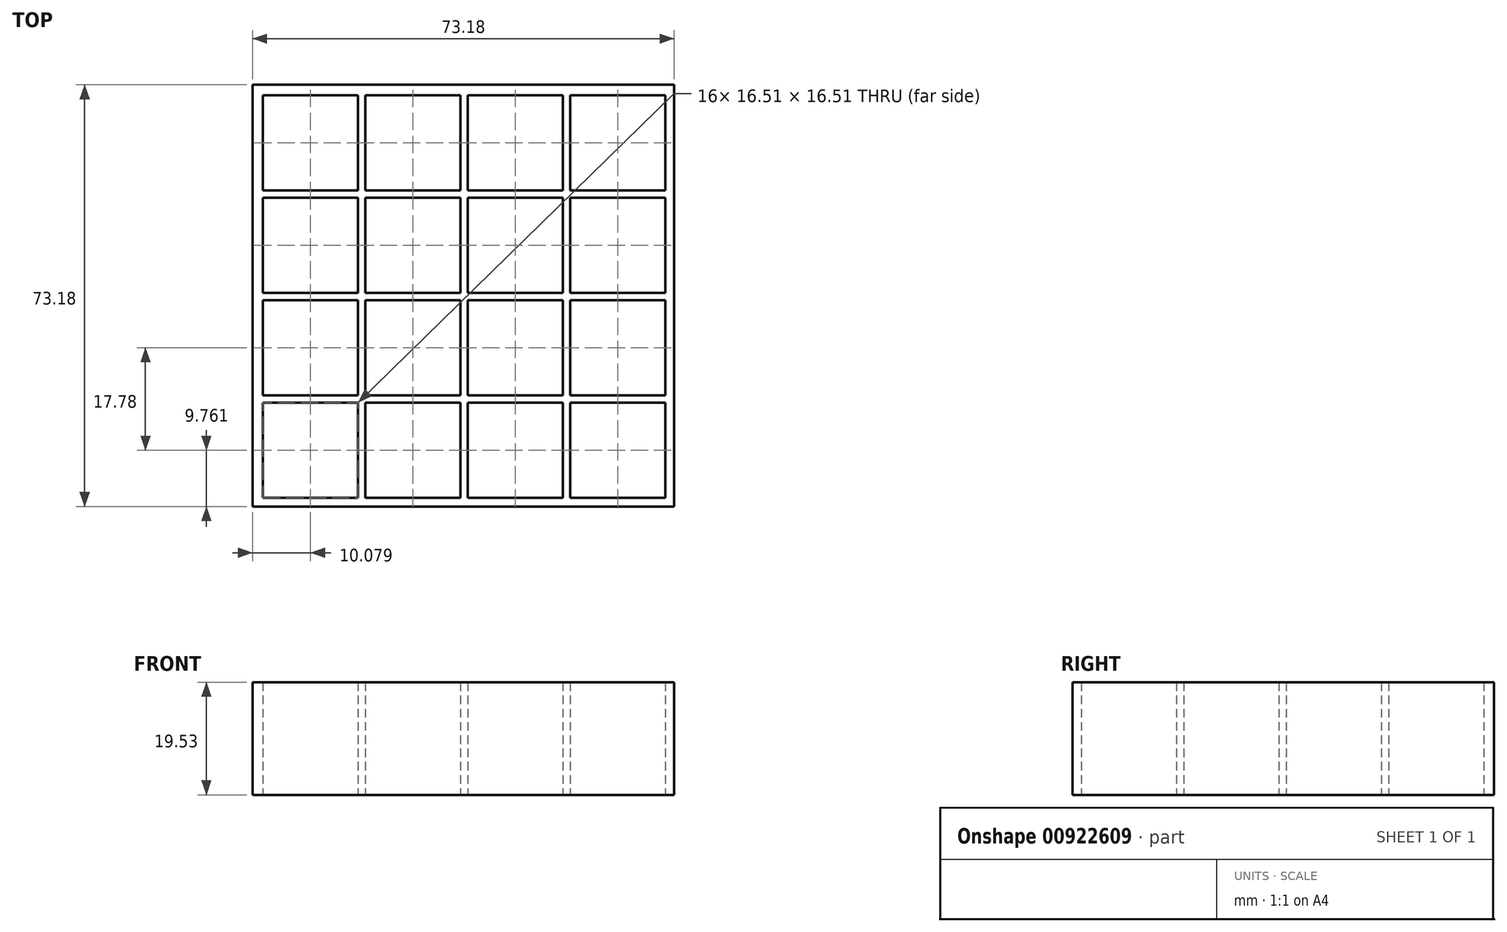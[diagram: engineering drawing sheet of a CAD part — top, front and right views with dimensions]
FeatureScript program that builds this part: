
annotation { "Feature Type Name" : "Feature", "Feature Type Description" : "" }
export const myFeature = defineFeature(function(context is Context, id is Id, definition is map)
    precondition{}
    {
        {
            var Q0;
            Q0=qCreatedBy(makeId("Top.planeOp"),FACE);
            var sketch = newSketch(context, id + "F0", { "sketchPlane" : qUnion([Q0])});
            skLineSegment(sketch, "E0.bottom", {"start": v(-731.84, 731.84) * mm, "end": v(731.84, 731.84) * mm});
            skLineSegment(sketch, "E0.top", {"start": v(-731.84, -731.84) * mm, "end": v(731.84, -731.84) * mm});
            skLineSegment(sketch, "E0.left", {"start": v(-731.84, 731.84) * mm, "end": v(-731.84, -731.84) * mm});
            skLineSegment(sketch, "E0.right", {"start": v(731.84, 731.84) * mm, "end": v(731.84, -731.84) * mm});
            skPoint(sketch, "E0.middle", {"position": v(0, 0) * mm});
            skLineSegment(sketch, "E1.bottom", {"start": v(-695.33, 695.33) * mm, "end": v(-365.13, 695.33) * mm});
            skLineSegment(sketch, "E1.top", {"start": v(-695.32, 365.13) * mm, "end": v(-365.12, 365.13) * mm});
            skLineSegment(sketch, "E1.left", {"start": v(-695.32, 695.33) * mm, "end": v(-695.32, 365.13) * mm});
            skLineSegment(sketch, "E1.right", {"start": v(-365.12, 695.33) * mm, "end": v(-365.12, 365.13) * mm});
            skLineSegment(sketch, "E2.0.1.0", {"start": v(-695.32, 339.73) * mm, "end": v(-695.32, 9.53) * mm});
            skLineSegment(sketch, "E2.0.1.1", {"start": v(-695.33, 339.73) * mm, "end": v(-365.13, 339.73) * mm});
            skLineSegment(sketch, "E2.0.1.2", {"start": v(-365.12, 339.73) * mm, "end": v(-365.12, 9.53) * mm});
            skLineSegment(sketch, "E2.0.1.3", {"start": v(-695.32, 9.53) * mm, "end": v(-365.12, 9.53) * mm});
            skLineSegment(sketch, "E2.0.2.0", {"start": v(-695.32, -15.87) * mm, "end": v(-695.32, -346.07) * mm});
            skLineSegment(sketch, "E2.0.2.1", {"start": v(-695.33, -15.87) * mm, "end": v(-365.13, -15.87) * mm});
            skLineSegment(sketch, "E2.0.2.2", {"start": v(-365.12, -15.87) * mm, "end": v(-365.12, -346.07) * mm});
            skLineSegment(sketch, "E2.0.2.3", {"start": v(-695.32, -346.07) * mm, "end": v(-365.12, -346.07) * mm});
            skLineSegment(sketch, "E2.0.3.0", {"start": v(-695.32, -371.48) * mm, "end": v(-695.32, -701.68) * mm});
            skLineSegment(sketch, "E2.0.3.1", {"start": v(-695.33, -371.48) * mm, "end": v(-365.13, -371.48) * mm});
            skLineSegment(sketch, "E2.0.3.2", {"start": v(-365.12, -371.48) * mm, "end": v(-365.12, -701.68) * mm});
            skLineSegment(sketch, "E2.0.3.3", {"start": v(-695.32, -701.68) * mm, "end": v(-365.12, -701.68) * mm});
            skLineSegment(sketch, "E2.1.0.0", {"start": v(-339.72, 695.33) * mm, "end": v(-339.72, 365.13) * mm});
            skLineSegment(sketch, "E2.1.0.1", {"start": v(-339.73, 695.33) * mm, "end": v(-9.53, 695.33) * mm});
            skLineSegment(sketch, "E2.1.0.2", {"start": v(-9.52, 695.33) * mm, "end": v(-9.52, 365.13) * mm});
            skLineSegment(sketch, "E2.1.0.3", {"start": v(-339.72, 365.13) * mm, "end": v(-9.52, 365.13) * mm});
            skLineSegment(sketch, "E2.1.1.0", {"start": v(-339.72, 339.73) * mm, "end": v(-339.72, 9.53) * mm});
            skLineSegment(sketch, "E2.1.1.1", {"start": v(-339.73, 339.73) * mm, "end": v(-9.53, 339.73) * mm});
            skLineSegment(sketch, "E2.1.1.2", {"start": v(-9.52, 339.73) * mm, "end": v(-9.52, 9.53) * mm});
            skLineSegment(sketch, "E2.1.1.3", {"start": v(-339.72, 9.53) * mm, "end": v(-9.52, 9.53) * mm});
            skLineSegment(sketch, "E2.1.2.0", {"start": v(-339.72, -15.87) * mm, "end": v(-339.72, -346.07) * mm});
            skLineSegment(sketch, "E2.1.2.1", {"start": v(-339.73, -15.87) * mm, "end": v(-9.53, -15.87) * mm});
            skLineSegment(sketch, "E2.1.2.2", {"start": v(-9.52, -15.87) * mm, "end": v(-9.52, -346.07) * mm});
            skLineSegment(sketch, "E2.1.2.3", {"start": v(-339.72, -346.07) * mm, "end": v(-9.52, -346.07) * mm});
            skLineSegment(sketch, "E2.1.3.0", {"start": v(-339.72, -371.48) * mm, "end": v(-339.72, -701.68) * mm});
            skLineSegment(sketch, "E2.1.3.1", {"start": v(-339.73, -371.48) * mm, "end": v(-9.53, -371.48) * mm});
            skLineSegment(sketch, "E2.1.3.2", {"start": v(-9.52, -371.48) * mm, "end": v(-9.52, -701.68) * mm});
            skLineSegment(sketch, "E2.1.3.3", {"start": v(-339.72, -701.68) * mm, "end": v(-9.52, -701.68) * mm});
            skLineSegment(sketch, "E2.2.0.0", {"start": v(15.88, 695.33) * mm, "end": v(15.88, 365.13) * mm});
            skLineSegment(sketch, "E2.2.0.1", {"start": v(15.87, 695.33) * mm, "end": v(346.08, 695.33) * mm});
            skLineSegment(sketch, "E2.2.0.2", {"start": v(346.08, 695.33) * mm, "end": v(346.08, 365.13) * mm});
            skLineSegment(sketch, "E2.2.0.3", {"start": v(15.88, 365.13) * mm, "end": v(346.08, 365.13) * mm});
            skLineSegment(sketch, "E2.2.1.0", {"start": v(15.88, 339.73) * mm, "end": v(15.88, 9.53) * mm});
            skLineSegment(sketch, "E2.2.1.1", {"start": v(15.87, 339.73) * mm, "end": v(346.08, 339.73) * mm});
            skLineSegment(sketch, "E2.2.1.2", {"start": v(346.08, 339.73) * mm, "end": v(346.08, 9.53) * mm});
            skLineSegment(sketch, "E2.2.1.3", {"start": v(15.88, 9.53) * mm, "end": v(346.08, 9.53) * mm});
            skLineSegment(sketch, "E2.2.2.0", {"start": v(15.88, -15.87) * mm, "end": v(15.88, -346.07) * mm});
            skLineSegment(sketch, "E2.2.2.1", {"start": v(15.87, -15.87) * mm, "end": v(346.08, -15.87) * mm});
            skLineSegment(sketch, "E2.2.2.2", {"start": v(346.08, -15.87) * mm, "end": v(346.08, -346.07) * mm});
            skLineSegment(sketch, "E2.2.2.3", {"start": v(15.88, -346.07) * mm, "end": v(346.08, -346.07) * mm});
            skLineSegment(sketch, "E2.2.3.0", {"start": v(15.88, -371.48) * mm, "end": v(15.88, -701.68) * mm});
            skLineSegment(sketch, "E2.2.3.1", {"start": v(15.87, -371.48) * mm, "end": v(346.08, -371.48) * mm});
            skLineSegment(sketch, "E2.2.3.2", {"start": v(346.08, -371.48) * mm, "end": v(346.08, -701.68) * mm});
            skLineSegment(sketch, "E2.2.3.3", {"start": v(15.88, -701.68) * mm, "end": v(346.08, -701.68) * mm});
            skLineSegment(sketch, "E2.3.0.0", {"start": v(371.48, 695.33) * mm, "end": v(371.48, 365.13) * mm});
            skLineSegment(sketch, "E2.3.0.1", {"start": v(371.48, 695.33) * mm, "end": v(701.68, 695.33) * mm});
            skLineSegment(sketch, "E2.3.0.2", {"start": v(701.68, 695.33) * mm, "end": v(701.68, 365.13) * mm});
            skLineSegment(sketch, "E2.3.0.3", {"start": v(371.48, 365.13) * mm, "end": v(701.68, 365.13) * mm});
            skLineSegment(sketch, "E2.3.1.0", {"start": v(371.48, 339.73) * mm, "end": v(371.48, 9.53) * mm});
            skLineSegment(sketch, "E2.3.1.1", {"start": v(371.48, 339.73) * mm, "end": v(701.68, 339.73) * mm});
            skLineSegment(sketch, "E2.3.1.2", {"start": v(701.68, 339.73) * mm, "end": v(701.68, 9.53) * mm});
            skLineSegment(sketch, "E2.3.1.3", {"start": v(371.48, 9.53) * mm, "end": v(701.68, 9.53) * mm});
            skLineSegment(sketch, "E2.3.2.0", {"start": v(371.48, -15.87) * mm, "end": v(371.48, -346.07) * mm});
            skLineSegment(sketch, "E2.3.2.1", {"start": v(371.48, -15.87) * mm, "end": v(701.68, -15.87) * mm});
            skLineSegment(sketch, "E2.3.2.2", {"start": v(701.68, -15.87) * mm, "end": v(701.68, -346.07) * mm});
            skLineSegment(sketch, "E2.3.2.3", {"start": v(371.48, -346.07) * mm, "end": v(701.68, -346.07) * mm});
            skLineSegment(sketch, "E2.3.3.0", {"start": v(371.48, -371.48) * mm, "end": v(371.48, -701.68) * mm});
            skLineSegment(sketch, "E2.3.3.1", {"start": v(371.48, -371.48) * mm, "end": v(701.68, -371.48) * mm});
            skLineSegment(sketch, "E2.3.3.2", {"start": v(701.68, -371.48) * mm, "end": v(701.68, -701.68) * mm});
            skLineSegment(sketch, "E2.3.3.3", {"start": v(371.48, -701.68) * mm, "end": v(701.68, -701.68) * mm});
            skLineSegment(sketch, "E2.direction1", {"start": v(-695.32, 365.13) * mm, "end": v(-339.72, 365.13) * mm, "construction": true});
            skLineSegment(sketch, "E2.direction2", {"start": v(-695.32, 365.13) * mm, "end": v(-695.32, 9.53) * mm, "construction": true});
            skSolve(sketch);
        }
        {
            var Q0;
            Q0 = qSketchRegion(id + "F0", true);
            extrude(context, id + "F1", {"entities" : qUnion([Q0]), "depth" : 390.52 * mm, "offsetDistance" : 25.4 * mm});
        }
        {
            var Q0;
            Q0=makeQuery(id+"F1.opExtrude","SWEPT_BODY",BODY,{"disambiguationData":[OSD([sQuery(id+"F0.wireOp",EDGE,"E0.bottom"),sQuery(id+"F0.wireOp",EDGE,"E0.top"),sQuery(id+"F0.wireOp",EDGE,"E0.left"),sQuery(id+"F0.wireOp",EDGE,"E0.right"),sQuery(id+"F0.wireOp",EDGE,"E1.bottom"),sQuery(id+"F0.wireOp",EDGE,"E1.top"),sQuery(id+"F0.wireOp",EDGE,"E1.left"),sQuery(id+"F0.wireOp",EDGE,"E1.right"),sQuery(id+"F0.wireOp",EDGE,"E2.0.1.0"),sQuery(id+"F0.wireOp",EDGE,"E2.0.1.1"),sQuery(id+"F0.wireOp",EDGE,"E2.0.1.2"),sQuery(id+"F0.wireOp",EDGE,"E2.0.1.3"),sQuery(id+"F0.wireOp",EDGE,"E2.0.2.0"),sQuery(id+"F0.wireOp",EDGE,"E2.0.2.1"),sQuery(id+"F0.wireOp",EDGE,"E2.0.2.2"),sQuery(id+"F0.wireOp",EDGE,"E2.0.2.3"),sQuery(id+"F0.wireOp",EDGE,"E2.0.3.0"),sQuery(id+"F0.wireOp",EDGE,"E2.0.3.1"),sQuery(id+"F0.wireOp",EDGE,"E2.0.3.2"),sQuery(id+"F0.wireOp",EDGE,"E2.0.3.3"),sQuery(id+"F0.wireOp",EDGE,"E2.1.0.0"),sQuery(id+"F0.wireOp",EDGE,"E2.1.0.1"),sQuery(id+"F0.wireOp",EDGE,"E2.1.0.2"),sQuery(id+"F0.wireOp",EDGE,"E2.1.0.3"),sQuery(id+"F0.wireOp",EDGE,"E2.1.1.0"),sQuery(id+"F0.wireOp",EDGE,"E2.1.1.1"),sQuery(id+"F0.wireOp",EDGE,"E2.1.1.2"),sQuery(id+"F0.wireOp",EDGE,"E2.1.1.3"),sQuery(id+"F0.wireOp",EDGE,"E2.1.2.0"),sQuery(id+"F0.wireOp",EDGE,"E2.1.2.1"),sQuery(id+"F0.wireOp",EDGE,"E2.1.2.2"),sQuery(id+"F0.wireOp",EDGE,"E2.1.2.3"),sQuery(id+"F0.wireOp",EDGE,"E2.1.3.0"),sQuery(id+"F0.wireOp",EDGE,"E2.1.3.1"),sQuery(id+"F0.wireOp",EDGE,"E2.1.3.2"),sQuery(id+"F0.wireOp",EDGE,"E2.1.3.3"),sQuery(id+"F0.wireOp",EDGE,"E2.2.0.0"),sQuery(id+"F0.wireOp",EDGE,"E2.2.0.1"),sQuery(id+"F0.wireOp",EDGE,"E2.2.0.2"),sQuery(id+"F0.wireOp",EDGE,"E2.2.0.3"),sQuery(id+"F0.wireOp",EDGE,"E2.2.1.0"),sQuery(id+"F0.wireOp",EDGE,"E2.2.1.1"),sQuery(id+"F0.wireOp",EDGE,"E2.2.1.2"),sQuery(id+"F0.wireOp",EDGE,"E2.2.1.3"),sQuery(id+"F0.wireOp",EDGE,"E2.2.2.0"),sQuery(id+"F0.wireOp",EDGE,"E2.2.2.1"),sQuery(id+"F0.wireOp",EDGE,"E2.2.2.2"),sQuery(id+"F0.wireOp",EDGE,"E2.2.2.3"),sQuery(id+"F0.wireOp",EDGE,"E2.2.3.0"),sQuery(id+"F0.wireOp",EDGE,"E2.2.3.1"),sQuery(id+"F0.wireOp",EDGE,"E2.2.3.2"),sQuery(id+"F0.wireOp",EDGE,"E2.2.3.3"),sQuery(id+"F0.wireOp",EDGE,"E2.3.0.0"),sQuery(id+"F0.wireOp",EDGE,"E2.3.0.1"),sQuery(id+"F0.wireOp",EDGE,"E2.3.0.2"),sQuery(id+"F0.wireOp",EDGE,"E2.3.0.3"),sQuery(id+"F0.wireOp",EDGE,"E2.3.1.0"),sQuery(id+"F0.wireOp",EDGE,"E2.3.1.1"),sQuery(id+"F0.wireOp",EDGE,"E2.3.1.2"),sQuery(id+"F0.wireOp",EDGE,"E2.3.1.3"),sQuery(id+"F0.wireOp",EDGE,"E2.3.2.0"),sQuery(id+"F0.wireOp",EDGE,"E2.3.2.1"),sQuery(id+"F0.wireOp",EDGE,"E2.3.2.2"),sQuery(id+"F0.wireOp",EDGE,"E2.3.2.3"),sQuery(id+"F0.wireOp",EDGE,"E2.3.3.0"),sQuery(id+"F0.wireOp",EDGE,"E2.3.3.1"),sQuery(id+"F0.wireOp",EDGE,"E2.3.3.2"),sQuery(id+"F0.wireOp",EDGE,"E2.3.3.3")])]});
            var Q1;
            Q1=qCreatedBy(makeId("Origin.pointOp"),VERTEX);
            transform(context, id + "F2", {"entities" : qUnion([Q0]), "transformType" : TransformType.SCALE_UNIFORMLY, "scale" : 0.05, "scalePoint" : qUnion([Q1]), "makeCopy" : false});
        }
    });
